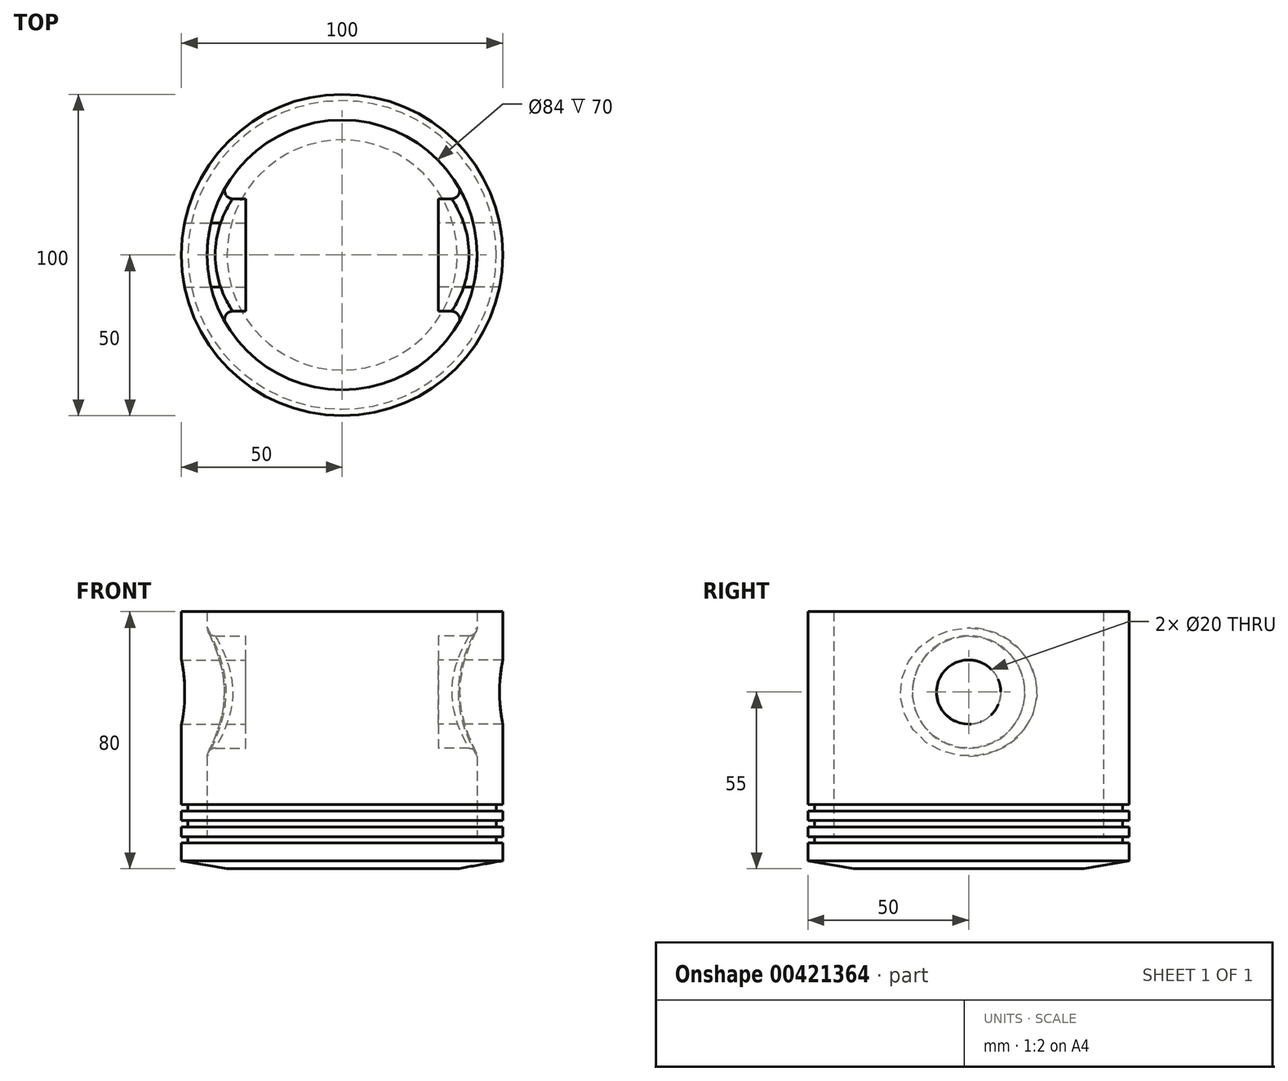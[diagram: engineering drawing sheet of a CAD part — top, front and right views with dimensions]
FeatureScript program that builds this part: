
annotation { "Feature Type Name" : "Feature", "Feature Type Description" : "" }
export const myFeature = defineFeature(function(context is Context, id is Id, definition is map)
    precondition{}
    {
        {
            var Q0;
            Q0=qCreatedBy(makeId("Top.planeOp"),FACE);
            var sketch = newSketch(context, id + "F0", { "sketchPlane" : qUnion([Q0])});
            skCircle(sketch, "E0", {"center": v(0, 0) * mm, "radius": 50 * mm});
            skCircle(sketch, "E1.0", {"center": v(0, 0) * mm, "radius": 42 * mm});
            skCircle(sketch, "E2.0", {"center": v(0, 0) * mm, "radius": 48 * mm});
            skSolve(sketch);
        }
        {
            var Q0;
            Q0=makeQuery(id+"F0.imprint","IMPRINT",FACE,{"disambiguationData":[TD([[makeQuery(id+"F0.imprint","IMPRINT",EDGE,{"derivedFrom":sQuery(id+"F0.wireOp",EDGE,"E0")}),1.0]])]});
            var Q1;
            Q1=makeQuery(id+"F0.imprint","IMPRINT",FACE,{"disambiguationData":[TD([[makeQuery(id+"F0.imprint","IMPRINT",EDGE,{"derivedFrom":sQuery(id+"F0.wireOp",EDGE,"E1.0")}),-1.0]])]});
            var Q2;
            Q2=makeQuery(id+"F0.imprint","IMPRINT",FACE,{"disambiguationData":[TD([[makeQuery(id+"F0.imprint","IMPRINT",EDGE,{"derivedFrom":sQuery(id+"F0.wireOp",EDGE,"E1.0")}),1.0]])]});
            extrude(context, id + "F1", {"entities" : qUnion([Q0, Q1, Q2]), "oppositeDirection" : true, "depth" : 10 * mm});
        }
        {
            var Q0;
            Q0=makeQuery(id+"F0.imprint","IMPRINT",FACE,{"disambiguationData":[TD([[makeQuery(id+"F0.imprint","IMPRINT",EDGE,{"derivedFrom":sQuery(id+"F0.wireOp",EDGE,"E1.0")}),-1.0]])]});
            var Q1;
            Q1=makeQuery(id+"F0.imprint","IMPRINT",FACE,{"disambiguationData":[TD([[makeQuery(id+"F0.imprint","IMPRINT",EDGE,{"derivedFrom":sQuery(id+"F0.wireOp",EDGE,"E0")}),1.0]])]});
            extrude(context, id + "F2", {"entities" : qUnion([Q0, Q1]), "operationType" : NewBodyOperationType.ADD, "depth" : 70 * mm});
        }
        {
            var Q0;
            Q0=makeQuery(id+"F0.imprint","IMPRINT",FACE,{"disambiguationData":[TD([[makeQuery(id+"F0.imprint","IMPRINT",EDGE,{"derivedFrom":sQuery(id+"F0.wireOp",EDGE,"E0")}),1.0]])]});
            extrude(context, id + "F3", {"entities" : qUnion([Q0]), "operationType" : NewBodyOperationType.REMOVE, "oppositeDirection" : true, "depth" : 2 * mm});
        }
        {
            var Q0;
            Q0=makeQuery(id+"F0.imprint","IMPRINT",FACE,{"disambiguationData":[TD([[makeQuery(id+"F0.imprint","IMPRINT",EDGE,{"derivedFrom":sQuery(id+"F0.wireOp",EDGE,"E0")}),1.0]])]});
            extrude(context, id + "F4", {"entities" : qUnion([Q0]), "operationType" : NewBodyOperationType.REMOVE, "depth" : 5 * mm, "hasSecondDirection" : true, "secondDirectionOppositeDirection" : false, "secondDirectionDepth" : 3 * mm});
        }
        {
            var Q0;
            Q0 = qSketchRegion(id + "F0", true);
            extrude(context, id + "F5", {"entities" : qUnion([Q0]), "operationType" : NewBodyOperationType.REMOVE, "depth" : 10 * mm, "hasSecondDirection" : true, "secondDirectionOppositeDirection" : false, "secondDirectionDepth" : 8 * mm});
        }
        {
            var Q0;
            Q0=makeQuery(id+"F1.opExtrude","CAP_EDGE",EDGE,{"disambiguationData":[OSD([sQuery(id+"F0.wireOp",EDGE,"E0")])],"isStart":false});
            chamfer(context, id + "F6", {"entities" : qUnion([Q0]), "chamferType" : ChamferType.OFFSET_ANGLE, "width" : 2.5 * mm, "oppositeDirection" : false, "angle" : 80 * degree, "tangentPropagation" : true});
        }
        {
            var Q0;
            Q0=qCreatedBy(makeId("Right.planeOp"),FACE);
            var sketch = newSketch(context, id + "F7", { "sketchPlane" : qUnion([Q0])});
            skCircle(sketch, "E3", {"center": v(0, 45) * mm, "radius": 10 * mm});
            skCircle(sketch, "E4", {"center": v(0, 45) * mm, "radius": 17.5 * mm});
            skSolve(sketch);
        }
        {
            var Q0;
            Q0=makeQuery(id+"F7.imprint","IMPRINT",FACE,{"disambiguationData":[TD([[makeQuery(id+"F7.imprint","IMPRINT",EDGE,{"derivedFrom":sQuery(id+"F7.wireOp",EDGE,"E3")}),-1.0]])]});
            extrude(context, id + "F8", {"entities" : qUnion([Q0]), "operationType" : NewBodyOperationType.ADD, "depth" : 45 * mm, "hasSecondDirection" : true, "secondDirectionOppositeDirection" : false, "secondDirectionDepth" : 30 * mm});
        }
        {
            var Q0;
            Q0 = qSketchRegion(id + "F7", true);
            extrude(context, id + "F9", {"entities" : qUnion([Q0]), "operationType" : NewBodyOperationType.ADD, "oppositeDirection" : true, "depth" : 45 * mm, "hasSecondDirection" : true, "secondDirectionOppositeDirection" : true, "secondDirectionDepth" : 30 * mm});
        }
        {
            var Q0;
            Q0=makeQuery(id+"F7.imprint","IMPRINT",FACE,{"disambiguationData":[TD([[makeQuery(id+"F7.imprint","IMPRINT",EDGE,{"derivedFrom":sQuery(id+"F7.wireOp",EDGE,"E3")}),1.0]])]});
            extrude(context, id + "F10", {"entities" : qUnion([Q0]), "operationType" : NewBodyOperationType.REMOVE, "endBound" : BoundingType.THROUGH_ALL, "oppositeDirection" : true, "depth" : 25 * mm, "hasSecondDirection" : true, "secondDirectionBound" : SecondDirectionBoundingType.THROUGH_ALL, "secondDirectionOppositeDirection" : false, "secondDirectionDepth" : 25 * mm});
        }
        {
            var Q0;
            Q0=makeQuery(id+"F2.opExtrude","CAP_EDGE",EDGE,{"disambiguationData":[OSD([sQuery(id+"F0.wireOp",EDGE,"E1.0")])],"isStart":true});
            var Q1;
            Q1=makeQuery(id+"F8.boolean.opBoolean","INTERSECT",EDGE,{"derivedFrom":[makeQuery(id+"F2.opExtrude","SWEPT_FACE",FACE,{"disambiguationData":[OSD([sQuery(id+"F0.wireOp",EDGE,"E1.0")])]}),makeQuery(id+"F8.opExtrude","SWEPT_FACE",FACE,{"disambiguationData":[OSD([sQuery(id+"F7.wireOp",EDGE,"E4")])]})]});
            var Q2;
            {var subQ0=sQuery(id+"F7.wireOp",EDGE,"E4");var subQ1=sQuery(id+"F0.wireOp",EDGE,"E0");var subQ2=sQuery(id+"F0.wireOp",EDGE,"E1.0");Q2=makeQuery(id+"F9.boolean.opBoolean","INTERSECT",EDGE,{"derivedFrom":[makeQuery(id+"F8.boolean.opBoolean","SPLIT",FACE,{"disambiguationData":[TD([makeQuery(id+"F1.opExtrude","CAP_FACE",FACE,{"disambiguationData":[OSD([subQ1])],"isStart":true})])],"derivedFrom":makeQuery(id+"F2.opExtrude","SWEPT_FACE",FACE,{"disambiguationData":[OSD([subQ2])]})}),makeQuery(id+"F9.opExtrude","SWEPT_FACE",FACE,{"disambiguationData":[OSD([subQ0])]})]});}
            fillet(context, id + "F11", {"entities" : qUnion([Q0, Q1, Q2]), "radius" : 2.5 * mm, "tangentPropagation" : true, "allowEdgeOverflow" : false});
        }
    });
